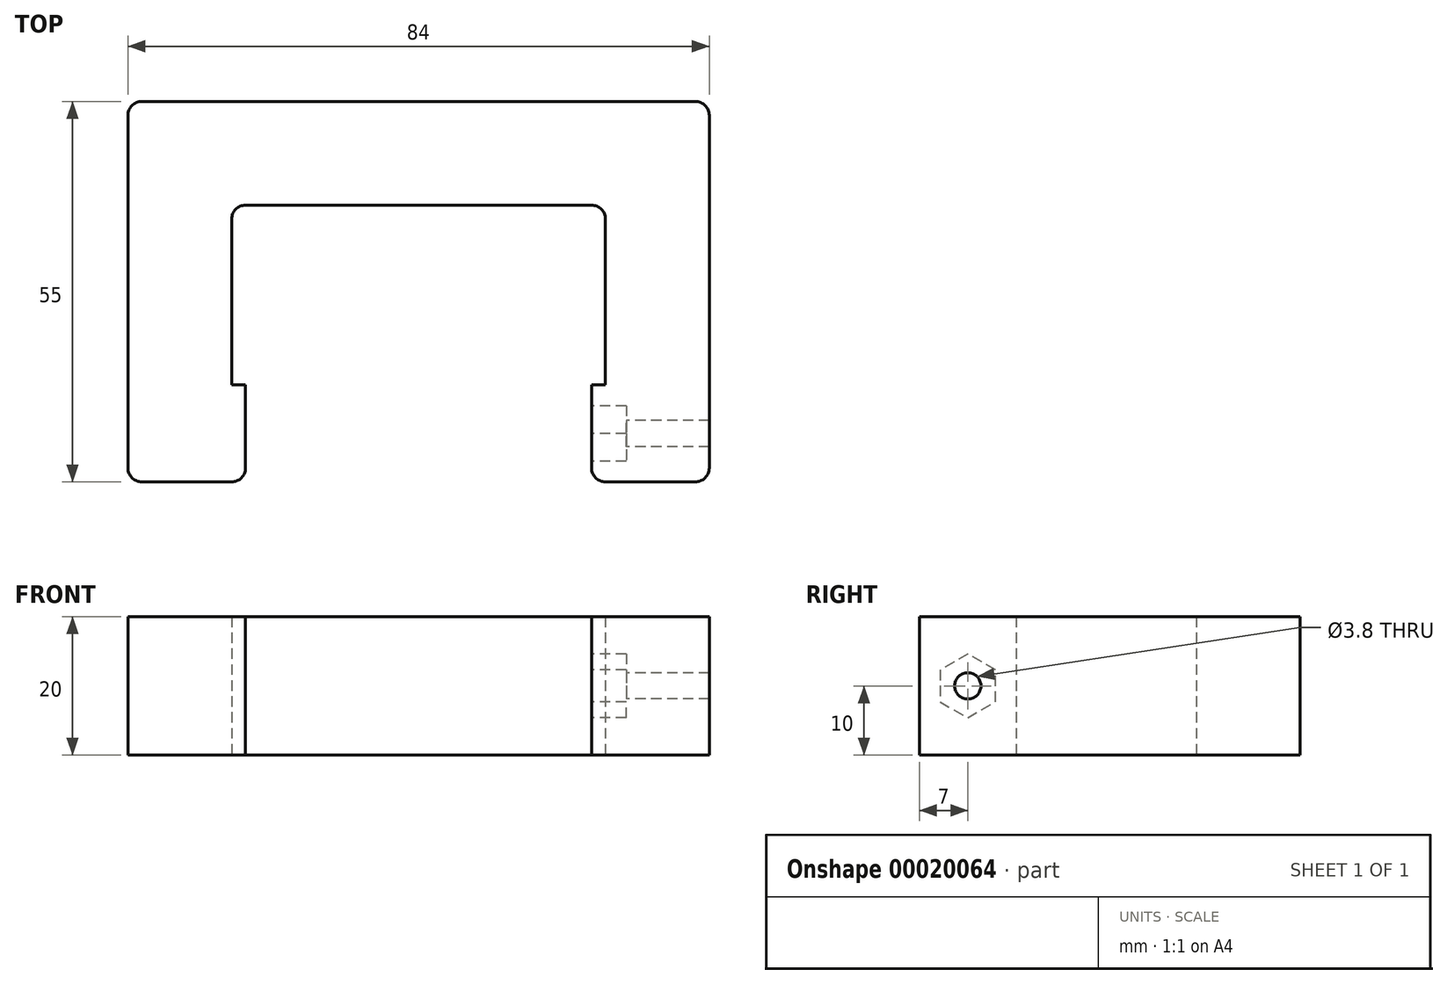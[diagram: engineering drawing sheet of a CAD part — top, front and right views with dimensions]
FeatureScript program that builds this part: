
annotation { "Feature Type Name" : "Feature", "Feature Type Description" : "" }
export const myFeature = defineFeature(function(context is Context, id is Id, definition is map)
    precondition{}
    {
        {
            var Q0;
            Q0=qCreatedBy(makeId("Top.planeOp"),FACE);
            var sketch = newSketch(context, id + "F0", { "sketchPlane" : qUnion([Q0])});
            skLineSegment(sketch, "E0.top", {"start": v(2, 40) * mm, "end": v(52, 40) * mm});
            skLineSegment(sketch, "E1.0", {"start": v(69, 2) * mm, "end": v(69, 43) * mm});
            skLineSegment(sketch, "E1.1", {"start": v(-13, 55) * mm, "end": v(57, 55) * mm});
            skLineSegment(sketch, "E1.2", {"start": v(-15, 2) * mm, "end": v(-15, 53) * mm});
            skLineSegment(sketch, "E2", {"start": v(-13, 0) * mm, "end": v(0, 0) * mm});
            skPoint(sketch, "E3.visualSharp", {"position": v(-15, 55) * mm});
            skArc(sketch, "E3.filletArc", {"start": v(-13, 55) * mm, "mid": v(-14.41, 54.41) * mm, "end": v(-15, 53) * mm});
            skPoint(sketch, "E4.visualSharp", {"position": v(69, 55) * mm});
            skPoint(sketch, "E5.visualSharp", {"position": v(5, 26.5) * mm});
            skPoint(sketch, "E6.visualSharp", {"position": v(5, 33) * mm});
            skPoint(sketch, "E7.visualSharp", {"position": v(48, 33) * mm});
            skPoint(sketch, "E8.visualSharp", {"position": v(48, 26.5) * mm});
            skPoint(sketch, "E9.visualSharp", {"position": v(0, 40) * mm});
            skArc(sketch, "E9.filletArc", {"start": v(2, 40) * mm, "mid": v(0.59, 39.41) * mm, "end": v(0, 38) * mm});
            skPoint(sketch, "E10.visualSharp", {"position": v(53, 40) * mm});
            skArc(sketch, "E10.filletArc", {"start": v(54, 38) * mm, "mid": v(53.41, 39.41) * mm, "end": v(52, 40) * mm});
            skPoint(sketch, "E11.visualSharp", {"position": v(54, 0) * mm});
            skPoint(sketch, "E12.visualSharp", {"position": v(69, 0) * mm});
            skPoint(sketch, "E13.visualSharp", {"position": v(-15, 0) * mm});
            skArc(sketch, "E13.filletArc", {"start": v(-15, 2) * mm, "mid": v(-14.41, 0.59) * mm, "end": v(-13, 0) * mm});
            skPoint(sketch, "E14.visualSharp", {"position": v(0, 0) * mm});
            skPoint(sketch, "E15.visualSharp", {"position": v(0, 33) * mm});
            skPoint(sketch, "E16.visualSharp", {"position": v(53, 33) * mm});
            skPoint(sketch, "E17.visualSharp", {"position": v(53, 26.5) * mm});
            skPoint(sketch, "E18.visualSharp", {"position": v(0, 14) * mm});
            skLineSegment(sketch, "E19", {"start": v(54, 14) * mm, "end": v(52, 14) * mm});
            skPoint(sketch, "E20.start.orphan", {"position": v(1.85, 14) * mm});
            skLineSegment(sketch, "E21", {"start": v(0, 38) * mm, "end": v(0, 14) * mm});
            skPoint(sketch, "E22.end.orphan", {"position": v(54, 2) * mm});
            skLineSegment(sketch, "E23", {"start": v(54, 38) * mm, "end": v(54, 14) * mm});
            skLineSegment(sketch, "E24", {"start": v(57, 0) * mm, "end": v(54, 0) * mm});
            skLineSegment(sketch, "E25", {"start": v(54, 0) * mm, "end": v(52, 0) * mm});
            skLineSegment(sketch, "E26", {"start": v(52, 14) * mm, "end": v(52, 0) * mm});
            skLineSegment(sketch, "E27", {"start": v(0, 0) * mm, "end": v(2, 0) * mm});
            skLineSegment(sketch, "E28", {"start": v(2, 0) * mm, "end": v(2, 14) * mm});
            skLineSegment(sketch, "E29", {"start": v(2, 14) * mm, "end": v(0, 14) * mm});
            skPoint(sketch, "E30.end.orphan", {"position": v(50.59, 2) * mm});
            skLineSegment(sketch, "E31", {"start": v(54, 0) * mm, "end": v(69, 0) * mm});
            skLineSegment(sketch, "E32", {"start": v(69, 0) * mm, "end": v(69, 43) * mm});
            skLineSegment(sketch, "E33", {"start": v(69, 43) * mm, "end": v(69, 55) * mm});
            skLineSegment(sketch, "E34", {"start": v(69, 55) * mm, "end": v(57, 55) * mm});
            skSolve(sketch);
        }
        {
            var Q0;
            Q0=makeQuery(id+"F0.imprint","IMPRINT",FACE,{"disambiguationData":[TD([[makeQuery(id+"F0.imprint","IMPRINT",EDGE,{"derivedFrom":sQuery(id+"F0.wireOp",EDGE,"E0.top")}),1.0]])]});
            extrude(context, id + "F1", {"entities" : qUnion([Q0]), "depth" : 20 * mm});
        }
        {
            var Q0;
            Q0=makeQuery(id+"F1.opExtrude","SWEPT_FACE",FACE,{"disambiguationData":[OSD([sQuery(id+"F0.wireOp",EDGE,"E26")])]});
            var sketch = newSketch(context, id + "F2", { "sketchPlane" : qUnion([Q0])});
            skCircle(sketch, "E35.cCircle", {"center": v(-7, 10) * mm, "radius": 4 * mm, "construction": true});
            skPoint(sketch, "E35.cCircle.centerSnap0", {"position": v(-7, 20) * mm});
            skPoint(sketch, "E35.cCircle.centerSnap1", {"position": v(-14, 10) * mm});
            skLineSegment(sketch, "E35.0", {"start": v(-3, 12.3) * mm, "end": v(-3, 7.7) * mm});
            skLineSegment(sketch, "E35.1", {"start": v(-3, 7.7) * mm, "end": v(-7, 5.38) * mm});
            skLineSegment(sketch, "E35.2", {"start": v(-7, 5.38) * mm, "end": v(-11, 7.7) * mm});
            skLineSegment(sketch, "E35.3", {"start": v(-11, 7.7) * mm, "end": v(-11, 12.3) * mm});
            skLineSegment(sketch, "E35.4", {"start": v(-11, 12.3) * mm, "end": v(-7, 14.62) * mm});
            skLineSegment(sketch, "E35.5", {"start": v(-7, 14.62) * mm, "end": v(-3, 12.3) * mm});
            skPoint(sketch, "E35.0.midPoint", {"position": v(-3, 10) * mm});
            skCircle(sketch, "E36", {"center": v(-7, 10) * mm, "radius": 1.9 * mm});
            skSolve(sketch);
        }
        {
            var Q0;
            Q0=makeQuery(id+"F2.imprint","IMPRINT",FACE,{"disambiguationData":[TD([[makeQuery(id+"F2.imprint","IMPRINT",EDGE,{"derivedFrom":sQuery(id+"F2.wireOp",EDGE,"E36")}),1.0]])]});
            extrude(context, id + "F3", {"entities" : qUnion([Q0]), "operationType" : NewBodyOperationType.REMOVE, "oppositeDirection" : true, "depth" : 25 * mm});
        }
        {
            var Q0;
            Q0=makeQuery(id+"F2.imprint","IMPRINT",FACE,{"disambiguationData":[TD([[makeQuery(id+"F2.imprint","IMPRINT",EDGE,{"derivedFrom":sQuery(id+"F2.wireOp",EDGE,"E35.0")}),-1.0]])]});
            extrude(context, id + "F4", {"entities" : qUnion([Q0]), "operationType" : NewBodyOperationType.REMOVE, "oppositeDirection" : true, "depth" : 5 * mm});
        }
        {
            var Q0;
            Q0=makeQuery(id+"FCJR9x0iEZllUuj_1.opExtrude","CAP_EDGE",EDGE,{"disambiguationData":[OSD([sQuery(id+"F0.wireOp",EDGE,"E33"),sQuery(id+"F0.wireOp",EDGE,"E34")])],"isStart":false});
            var Q1;
            Q1=makeQuery(id+"FCJR9x0iEZllUuj_1.opExtrude","CAP_EDGE",EDGE,{"disambiguationData":[OSD([sQuery(id+"F0.wireOp",EDGE,"E31"),sQuery(id+"F0.wireOp",EDGE,"E32")])],"isStart":false});
            var Q2;
            Q2=makeQuery(id+"F1.opExtrude","SWEPT_EDGE",EDGE,{"disambiguationData":[OSD([sQuery(id+"F0.wireOp",EDGE,"E25"),sQuery(id+"F0.wireOp",EDGE,"E26")])]});
            var Q3;
            Q3=makeQuery(id+"F1.opExtrude","SWEPT_EDGE",EDGE,{"disambiguationData":[OSD([sQuery(id+"F0.wireOp",EDGE,"E27"),sQuery(id+"F0.wireOp",EDGE,"E28")])]});
            fillet(context, id + "F5", {"entities" : qUnion([Q0, Q1, Q2, Q3]), "radius" : 2 * mm, "tangentPropagation" : true, "allowEdgeOverflow" : false});
        }
        {
            var Q0;
            Q0=makeQuery(id+"F1.opExtrude","SWEPT_EDGE",EDGE,{"disambiguationData":[OSD([sQuery(id+"F0.wireOp",EDGE,"E33"),sQuery(id+"F0.wireOp",EDGE,"E34")])]});
            var Q1;
            Q1=makeQuery(id+"F1.opExtrude","SWEPT_EDGE",EDGE,{"disambiguationData":[OSD([sQuery(id+"F0.wireOp",EDGE,"E31"),sQuery(id+"F0.wireOp",EDGE,"E32")])]});
            fillet(context, id + "F6", {"entities" : qUnion([Q0, Q1]), "radius" : 2 * mm, "tangentPropagation" : true, "allowEdgeOverflow" : false});
        }
    });
